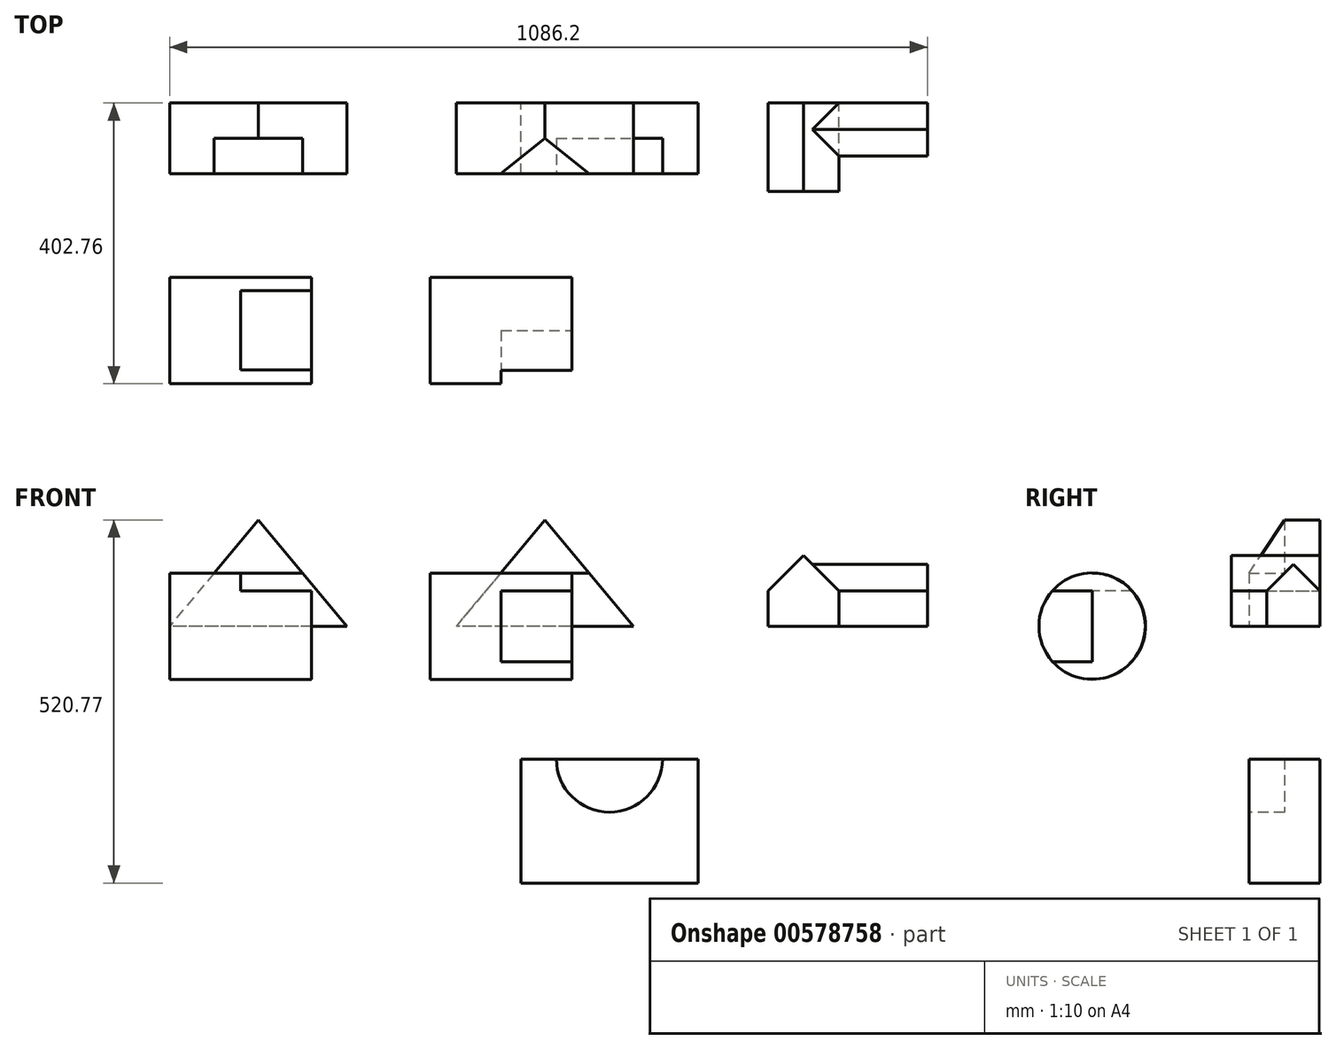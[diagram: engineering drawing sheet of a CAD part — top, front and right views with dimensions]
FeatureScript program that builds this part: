
annotation { "Feature Type Name" : "Feature", "Feature Type Description" : "" }
export const myFeature = defineFeature(function(context is Context, id is Id, definition is map)
    precondition{}
    {
        {
            var Q0;
            Q0=qCreatedBy(makeId("Front.planeOp"),FACE);
            var sketch = newSketch(context, id + "F0", { "sketchPlane" : qUnion([Q0])});
            skLineSegment(sketch, "E0", {"start": v(254, 0) * mm, "end": v(0, 0) * mm});
            skLineSegment(sketch, "E1", {"start": v(0, 0) * mm, "end": v(127, 0) * mm});
            skLineSegment(sketch, "E2", {"start": v(127, 152.4) * mm, "end": v(0, 0) * mm});
            skLineSegment(sketch, "E3", {"start": v(127, 152.4) * mm, "end": v(254, 0) * mm});
            skLineSegment(sketch, "E4", {"start": v(63.5, 76.2) * mm, "end": v(190.5, 76.2) * mm});
            skSolve(sketch);
        }
        {
            var Q0;
            {var subQ4=sQuery(id+"F0.wireOp",EDGE,"E0");Q0=makeQuery(id+"F0.imprint","IMPRINT",FACE,{"disambiguationData":[TD([[makeQuery(id+"F0.imprint","IMPRINT",EDGE,{"derivedFrom":subQ4}),-1.0]])]});}
            extrude(context, id + "F1", {"entities" : qUnion([Q0]), "depth" : 101.6 * mm, "offsetDistance" : 25.4 * mm});
        }
        {
            var Q0;
            Q0 = qSketchRegion(id + "F0", true);
            extrude(context, id + "F2", {"entities" : qUnion([Q0]), "operationType" : NewBodyOperationType.ADD, "depth" : 50.8 * mm, "offsetDistance" : 25.4 * mm});
        }
        {
            var Q0;
            Q0=qCreatedBy(makeId("Front.planeOp"),FACE);
            var sketch = newSketch(context, id + "F3", { "sketchPlane" : qUnion([Q0])});
            skLineSegment(sketch, "E5", {"start": v(664.78, 0) * mm, "end": v(410.78, 0) * mm});
            skLineSegment(sketch, "E6", {"start": v(537.78, 152.4) * mm, "end": v(410.78, 0) * mm});
            skLineSegment(sketch, "E7", {"start": v(537.78, 152.4) * mm, "end": v(664.78, 0) * mm});
            skLineSegment(sketch, "E8", {"start": v(474.28, 76.2) * mm, "end": v(601.28, 76.2) * mm});
            skSolve(sketch);
        }
        {
            var Q0;
            {var subQ3=sQuery(id+"F3.wireOp",EDGE,"E8");Q0=makeQuery(id+"F3.imprint","IMPRINT",FACE,{"disambiguationData":[TD([[makeQuery(id+"F3.imprint","IMPRINT",EDGE,{"derivedFrom":subQ3}),1.0]])]});}
            extrude(context, id + "F4", {"entities" : qUnion([Q0]), "depth" : 101.6 * mm, "offsetDistance" : 25.4 * mm});
        }
        {
            var Q0;
            Q0 = qSketchRegion(id + "F3", true);
            extrude(context, id + "F5", {"entities" : qUnion([Q0]), "operationType" : NewBodyOperationType.ADD, "depth" : 101.6 * mm, "offsetDistance" : 25.4 * mm});
        }
        {
            var Q0;
            Q0=makeQuery(id+"F5.opExtrude","CAP_EDGE",EDGE,{"disambiguationData":[OSD([sQuery(id+"F3.wireOp",EDGE,"E5")])],"isStart":false});
            cPoint(context, id + "F6", {"entities" : qUnion([Q0]), "parameter" : 0.5});
        }
        {
            var Q0;
            Q0=makeQuery(id+"F4.opExtrude","CAP_VERTEX",VERTEX,{"disambiguationData":[OSD([sQuery(id+"F3.wireOp",EDGE,"E6"),sQuery(id+"F3.wireOp",EDGE,"E7")])],"isStart":false});
            var Q1;
            Q1=makeQuery(id+"F4.opExtrude","CAP_VERTEX",VERTEX,{"disambiguationData":[OSD([sQuery(id+"F3.wireOp",EDGE,"E6"),sQuery(id+"F3.wireOp",EDGE,"E7")])],"isStart":true});
            var Q2;
            Q2 = qCreatedBy(id + "F6" ,VERTEX);
            cPlane(context, id + "F7", {"entities" : qUnion([Q0, Q1, Q2]), "cplaneType" : CPlaneType.THREE_POINT, "offset" : 25.4 * mm, "width" : 152.4 * mm, "height" : 152.4 * mm});
        }
        {
            var Q0;
            Q0=qCreatedBy(id+"F7.planeOp",FACE);
            var sketch = newSketch(context, id + "F8", { "sketchPlane" : qUnion([Q0])});
            skPoint(sketch, "E9.0", {"position": v(-101.6, 152.4) * mm});
            skPoint(sketch, "E10.0", {"position": v(-50.8, 152.4) * mm});
            skPoint(sketch, "E11.0", {"position": v(0, 152.4) * mm});
            skPoint(sketch, "E12.0", {"position": v(0, 0) * mm});
            skLineSegment(sketch, "E13.0", {"start": v(-101.6, 152.4) * mm, "end": v(-101.6, 0) * mm});
            skLineSegment(sketch, "E14", {"start": v(-101.6, 152.4) * mm, "end": v(-50.8, 152.4) * mm});
            skLineSegment(sketch, "E15", {"start": v(-50.8, 152.4) * mm, "end": v(-101.6, 76.2) * mm});
            skLineSegment(sketch, "E16", {"start": v(-101.6, 76.2) * mm, "end": v(-101.6, 152.4) * mm});
            skSolve(sketch);
        }
        {
            var Q0;
            Q0 = qSketchRegion(id + "F8", true);
            extrude(context, id + "F9", {"entities" : qUnion([Q0]), "operationType" : NewBodyOperationType.REMOVE, "endBound" : BoundingType.SYMMETRIC, "depth" : 127 * mm, "offsetDistance" : 25.4 * mm});
        }
        {
            var Q0;
            Q0=qCreatedBy(makeId("Front.planeOp"),FACE);
            var sketch = newSketch(context, id + "F10", { "sketchPlane" : qUnion([Q0])});
            skLineSegment(sketch, "E17", {"start": v(857.6, 0) * mm, "end": v(959.2, 0) * mm});
            skLineSegment(sketch, "E18", {"start": v(959.2, 0) * mm, "end": v(959.2, 50.8) * mm});
            skLineSegment(sketch, "E19", {"start": v(959.2, 50.8) * mm, "end": v(908.4, 101.6) * mm});
            skPoint(sketch, "E19.endSnap0", {"position": v(908.4, 0) * mm});
            skLineSegment(sketch, "E20", {"start": v(908.4, 101.6) * mm, "end": v(857.6, 50.8) * mm});
            skLineSegment(sketch, "E21", {"start": v(857.6, 50.8) * mm, "end": v(857.6, 0) * mm});
            skSolve(sketch);
        }
        {
            var Q0;
            Q0=makeQuery(id+"F10.imprint","IMPRINT",FACE,{"disambiguationData":[TD([[makeQuery(id+"F10.imprint","IMPRINT",EDGE,{"derivedFrom":sQuery(id+"F10.wireOp",EDGE,"E17")}),1.0]])]});
            extrude(context, id + "F11", {"entities" : qUnion([Q0]), "depth" : 127 * mm, "offsetDistance" : 25.4 * mm});
        }
        {
            var Q0;
            Q0=makeQuery(id+"F11.opExtrude","SWEPT_FACE",FACE,{"disambiguationData":[OSD([sQuery(id+"F10.wireOp",EDGE,"E18")])]});
            cPlane(context, id + "F12", {"entities" : qUnion([Q0]), "cplaneType" : CPlaneType.OFFSET, "offset" : 127 * mm, "width" : 152.4 * mm, "height" : 152.4 * mm});
        }
        {
            var Q0;
            Q0=qCreatedBy(id+"F12.planeOp",FACE);
            var sketch = newSketch(context, id + "F13", { "sketchPlane" : qUnion([Q0])});
            skLineSegment(sketch, "E22", {"start": v(0, 0) * mm, "end": v(-76.2, 0) * mm});
            skLineSegment(sketch, "E23", {"start": v(-76.2, 0) * mm, "end": v(-76.2, 50.8) * mm});
            skLineSegment(sketch, "E24", {"start": v(-76.2, 50.8) * mm, "end": v(-38.1, 88.9) * mm});
            skLineSegment(sketch, "E25", {"start": v(-38.1, 88.9) * mm, "end": v(0, 50.8) * mm});
            skLineSegment(sketch, "E26", {"start": v(0, 50.8) * mm, "end": v(0, 0) * mm});
            skPoint(sketch, "E27", {"position": v(-38.1, 0) * mm});
            skSolve(sketch);
        }
        {
            var Q0;
            Q0=makeQuery(id+"F13.imprint","IMPRINT",FACE,{"disambiguationData":[TD([[makeQuery(id+"F13.imprint","IMPRINT",EDGE,{"derivedFrom":sQuery(id+"F13.wireOp",EDGE,"E22")}),-1.0]])]});
            extrude(context, id + "F14", {"entities" : qUnion([Q0]), "endBound" : BoundingType.UP_TO_NEXT, "oppositeDirection" : true, "depth" : 25.4 * mm, "offsetDistance" : 25.4 * mm});
        }
        {
            var Q0;
            Q0=qCreatedBy(makeId("Right.planeOp"),FACE);
            var sketch = newSketch(context, id + "F15", { "sketchPlane" : qUnion([Q0])});
            skCircle(sketch, "E28", {"center": v(-326.19, 0) * mm, "radius": 76.2 * mm});
            skSolve(sketch);
        }
        {
            var Q0;
            Q0=makeQuery(id+"F15.imprint","IMPRINT",FACE,{"disambiguationData":[TD([[makeQuery(id+"F15.imprint","IMPRINT",EDGE,{"derivedFrom":sQuery(id+"F15.wireOp",EDGE,"E28")}),1.0]])]});
            extrude(context, id + "F16", {"entities" : qUnion([Q0]), "depth" : 203.2 * mm, "offsetDistance" : 25.4 * mm});
        }
        {
            var Q0;
            Q0=makeQuery(id+"F16.opExtrude","CAP_FACE",FACE,{"disambiguationData":[OSD([sQuery(id+"F15.wireOp",EDGE,"E28")])],"isStart":false});
            var sketch = newSketch(context, id + "F17", { "sketchPlane" : qUnion([Q0])});
            skLineSegment(sketch, "E29", {"start": v(-326.19, 50.8) * mm, "end": v(-382.98, 50.8) * mm});
            skLineSegment(sketch, "E30", {"start": v(-326.19, 50.8) * mm, "end": v(-269.39, 50.8) * mm});
            skPoint(sketch, "E31.orphan", {"position": v(-326.19, 0) * mm});
            skSolve(sketch);
        }
        {
            var Q0;
            {var subQ0=sQuery(id+"F17.wireOp",EDGE,"E29");Q0=makeQuery(id+"F17.imprint","IMPRINT",FACE,{"disambiguationData":[TD([[makeQuery(id+"F17.imprint","IMPRINT",EDGE,{"derivedFrom":subQ0}),-1.0]])]});}
            extrude(context, id + "F18", {"entities" : qUnion([Q0]), "operationType" : NewBodyOperationType.REMOVE, "oppositeDirection" : true, "depth" : 101.6 * mm, "offsetDistance" : 25.4 * mm});
        }
        {
            var Q0;
            Q0=makeQuery(id+"F16.opExtrude","CAP_FACE",FACE,{"disambiguationData":[OSD([sQuery(id+"F15.wireOp",EDGE,"E28")])],"isStart":false});
            cPlane(context, id + "F19", {"entities" : qUnion([Q0]), "cplaneType" : CPlaneType.OFFSET, "offset" : 170.18 * mm, "width" : 152.4 * mm, "height" : 152.4 * mm});
        }
        {
            var Q0;
            Q0=qCreatedBy(id+"F19.planeOp",FACE);
            var sketch = newSketch(context, id + "F20", { "sketchPlane" : qUnion([Q0])});
            skCircle(sketch, "E32", {"center": v(-326.56, 0) * mm, "radius": 76.2 * mm});
            skSolve(sketch);
        }
        {
            var Q0;
            Q0=makeQuery(id+"F20.imprint","IMPRINT",FACE,{"disambiguationData":[TD([[makeQuery(id+"F20.imprint","IMPRINT",EDGE,{"derivedFrom":sQuery(id+"F20.wireOp",EDGE,"E32")}),1.0]])]});
            extrude(context, id + "F21", {"entities" : qUnion([Q0]), "depth" : 203.2 * mm, "offsetDistance" : 25.4 * mm});
        }
        {
            var Q0;
            Q0=makeQuery(id+"F21.opExtrude","CAP_FACE",FACE,{"disambiguationData":[OSD([sQuery(id+"F20.wireOp",EDGE,"E32")])],"isStart":false});
            var sketch = newSketch(context, id + "F22", { "sketchPlane" : qUnion([Q0])});
            skLineSegment(sketch, "E33", {"start": v(-326.56, 0) * mm, "end": v(-326.56, 50.8) * mm});
            skLineSegment(sketch, "E34", {"start": v(-326.56, 50.8) * mm, "end": v(-383.35, 50.8) * mm});
            skLineSegment(sketch, "E35", {"start": v(-326.56, 0) * mm, "end": v(-326.56, -50.8) * mm});
            skLineSegment(sketch, "E36", {"start": v(-326.56, -50.8) * mm, "end": v(-383.35, -50.8) * mm});
            skSolve(sketch);
        }
        {
            var Q0;
            Q0=makeQuery(id+"F22.imprint","IMPRINT",FACE,{"disambiguationData":[TD([[makeQuery(id+"F22.imprint","IMPRINT",EDGE,{"derivedFrom":sQuery(id+"F22.wireOp",EDGE,"E33")}),1.0]])]});
            extrude(context, id + "F23", {"entities" : qUnion([Q0]), "operationType" : NewBodyOperationType.REMOVE, "oppositeDirection" : true, "depth" : 101.6 * mm, "offsetDistance" : 25.4 * mm});
        }
        {
            var Q0;
            Q0=qCreatedBy(makeId("Front.planeOp"),FACE);
            var sketch = newSketch(context, id + "F24", { "sketchPlane" : qUnion([Q0])});
            skLineSegment(sketch, "E37.bottom", {"start": v(503.44, -190.57) * mm, "end": v(757.44, -190.57) * mm});
            skLineSegment(sketch, "E37.top", {"start": v(503.44, -368.37) * mm, "end": v(757.44, -368.37) * mm});
            skLineSegment(sketch, "E37.left", {"start": v(503.44, -190.57) * mm, "end": v(503.44, -368.37) * mm});
            skLineSegment(sketch, "E37.right", {"start": v(757.44, -190.57) * mm, "end": v(757.44, -368.37) * mm});
            skSolve(sketch);
        }
        {
            var Q0;
            Q0=makeQuery(id+"F24.imprint","IMPRINT",FACE,{"disambiguationData":[TD([[makeQuery(id+"F24.imprint","IMPRINT",EDGE,{"derivedFrom":sQuery(id+"F24.wireOp",EDGE,"E37.bottom")}),-1.0]])]});
            extrude(context, id + "F25", {"entities" : qUnion([Q0]), "depth" : 101.6 * mm, "offsetDistance" : 25.4 * mm});
        }
        {
            var Q0;
            Q0=makeQuery(id+"F25.opExtrude","CAP_FACE",FACE,{"disambiguationData":[OSD([sQuery(id+"F24.wireOp",EDGE,"E37.bottom"),sQuery(id+"F24.wireOp",EDGE,"E37.top"),sQuery(id+"F24.wireOp",EDGE,"E37.left"),sQuery(id+"F24.wireOp",EDGE,"E37.right")])],"isStart":false});
            var sketch = newSketch(context, id + "F26", { "sketchPlane" : qUnion([Q0])});
            skArc(sketch, "E38", {"start": v(554.24, -190.57) * mm, "mid": v(630.44, -266.77) * mm, "end": v(706.64, -190.57) * mm});
            skSolve(sketch);
        }
        {
            var Q0;
            {var subQ0=sQuery(id+"F26.wireOp",EDGE,"E38");Q0=makeQuery(id+"F26.imprint","IMPRINT",FACE,{"disambiguationData":[TD([[makeQuery(id+"F26.imprint","IMPRINT",EDGE,{"derivedFrom":subQ0}),1.0]])]});}
            extrude(context, id + "F27", {"entities" : qUnion([Q0]), "operationType" : NewBodyOperationType.REMOVE, "oppositeDirection" : true, "depth" : 50.8 * mm, "offsetDistance" : 25.4 * mm});
        }
    });
